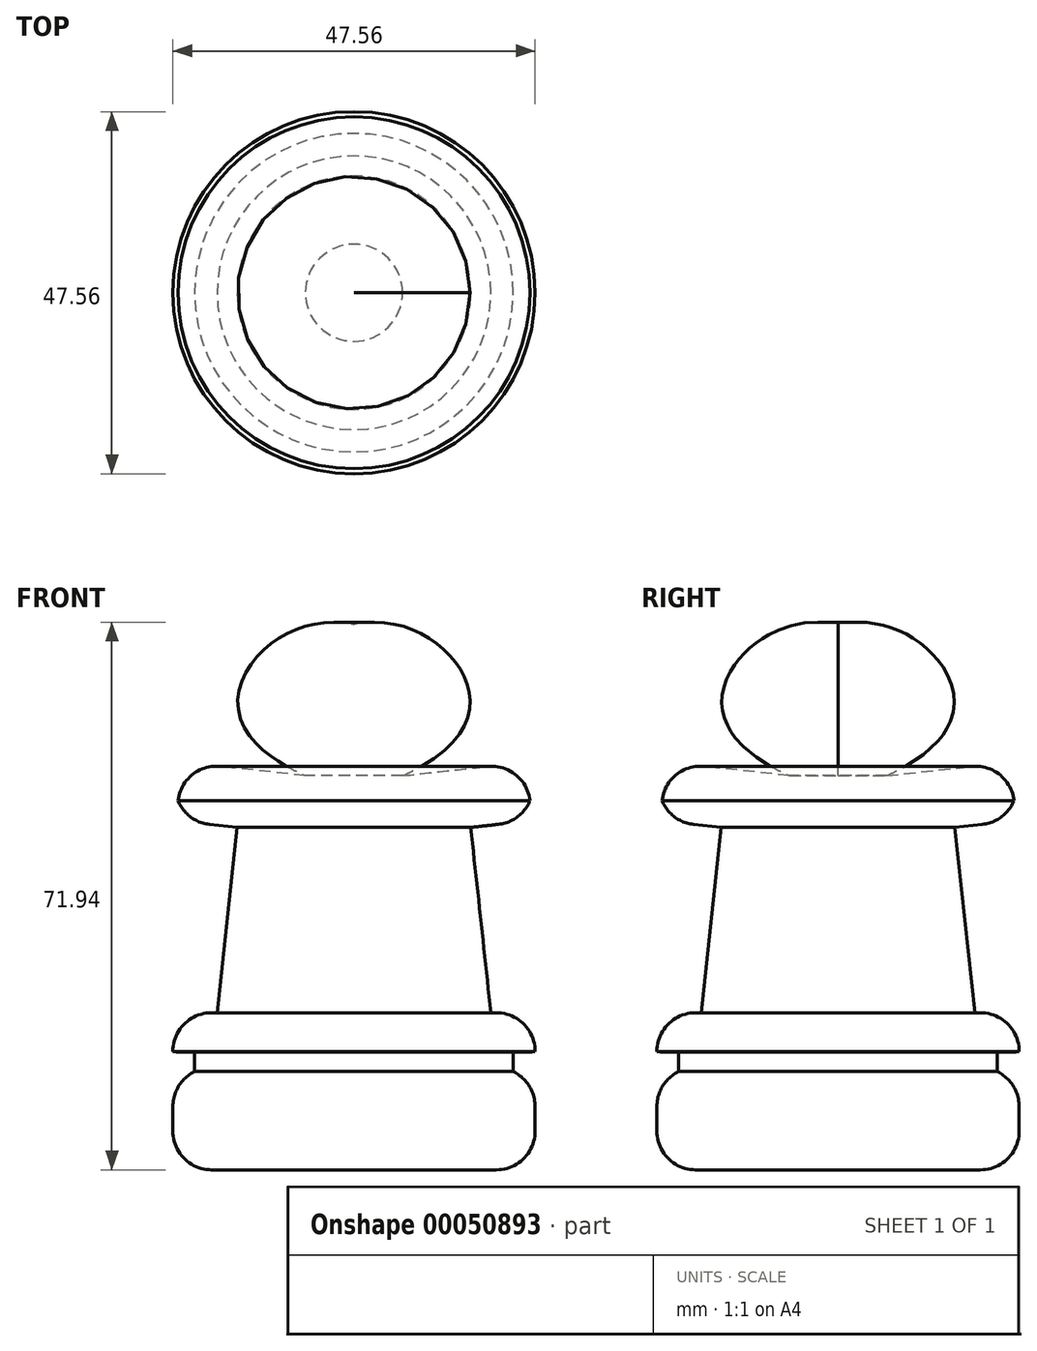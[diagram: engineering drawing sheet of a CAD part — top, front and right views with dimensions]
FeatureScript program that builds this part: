
annotation { "Feature Type Name" : "Feature", "Feature Type Description" : "" }
export const myFeature = defineFeature(function(context is Context, id is Id, definition is map)
    precondition{}
    {
        {
            var Q0;
            Q0=qCreatedBy(makeId("Front.planeOp"),FACE);
            var sketch = newSketch(context, id + "F0", { "sketchPlane" : qUnion([Q0])});
            skLineSegment(sketch, "E0", {"start": v(0, -65.77) * mm, "end": v(23.78, -65.77) * mm});
            skLineSegment(sketch, "E1", {"start": v(23.78, -65.77) * mm, "end": v(23.78, -52.87) * mm});
            skLineSegment(sketch, "E2", {"start": v(23.78, -52.87) * mm, "end": v(20.92, -52.87) * mm});
            skLineSegment(sketch, "E3", {"start": v(20.92, -52.87) * mm, "end": v(20.92, -50.3) * mm});
            skLineSegment(sketch, "E4", {"start": v(20.92, -50.3) * mm, "end": v(23.78, -50.3) * mm});
            skLineSegment(sketch, "E5", {"start": v(23.78, -50.3) * mm, "end": v(23.78, -45.13) * mm});
            skLineSegment(sketch, "E6", {"start": v(23.78, -45.13) * mm, "end": v(17.97, -45.13) * mm});
            skLineSegment(sketch, "E7", {"start": v(17.97, -45.13) * mm, "end": v(15.33, -20.78) * mm});
            skLineSegment(sketch, "E8", {"start": v(15.33, -20.78) * mm, "end": v(23.4, -19.9) * mm});
            skLineSegment(sketch, "E9", {"start": v(23.4, -19.9) * mm, "end": v(22.56, -12.23) * mm});
            skLineSegment(sketch, "E10", {"start": v(22.56, -12.23) * mm, "end": v(6.38, -13.99) * mm});
            skFitSpline(sketch, "E11", {"points": [v(6.38, -13.99) * mm, v(13.95, 0) * mm, v(0, 5.9) * mm], "startDerivative": vector(56.44, 25.22) * mm, "endDerivative": vector(-35.07, -7.52) * mm});
            skLineSegment(sketch, "E12", {"start": v(0, 5.9) * mm, "end": v(0, -65.77) * mm});
            skSolve(sketch);
        }
        {
            var Q0;
            Q0=makeQuery(id+"F0.imprint","IMPRINT",FACE,{"disambiguationData":[TD([[makeQuery(id+"F0.imprint","IMPRINT",EDGE,{"derivedFrom":sQuery(id+"F0.wireOp",EDGE,"E0")}),1.0]])]});
            var Q1;
            Q1=sQuery(id+"F0.wireOp",EDGE,"E6");
            var Q2;
            Q2=sQuery(id+"F0.wireOp",EDGE,"E5");
            var Q3;
            Q3=sQuery(id+"F0.wireOp",EDGE,"E0");
            var Q4;
            Q4=sQuery(id+"F0.wireOp",EDGE,"E1");
            var Q5;
            Q5=sQuery(id+"F0.wireOp",EDGE,"E12");
            var Q6;
            Q6=sQuery(id+"F0.wireOp",EDGE,"E11");
            var Q7;
            Q7=sQuery(id+"F0.wireOp",EDGE,"E10");
            var Q8;
            Q8=sQuery(id+"F0.wireOp",EDGE,"E9");
            var Q9;
            Q9=sQuery(id+"F0.wireOp",EDGE,"E8");
            var Q10;
            Q10=sQuery(id+"F0.wireOp",EDGE,"E7");
            var Q11;
            Q11=sQuery(id+"F0.wireOp",EDGE,"E4");
            var Q12;
            Q12=sQuery(id+"F0.wireOp",EDGE,"E3");
            var Q13;
            Q13=sQuery(id+"F0.wireOp",EDGE,"E2");
            var Q14;
            Q14=sQuery(id+"F0.wireOp",EDGE,"E12");
            revolve(context, id + "F1", {"entities" : qUnion([Q0]), "surfaceEntities" : qUnion([Q1, Q2, Q3, Q4, Q5, Q6, Q7, Q8, Q9, Q10, Q11, Q12, Q13]), "axis" : qUnion([Q14]), "revolveType" : RevolveType.FULL});
        }
        {
            var Q0;
            Q0=makeQuery(id+"F1.opRevolve","SWEPT_EDGE",EDGE,{"disambiguationData":[OSD([sQuery(id+"F0.wireOp",EDGE,"E9"),sQuery(id+"F0.wireOp",EDGE,"E10")])]});
            fillet(context, id + "F2", {"entities" : qUnion([Q0]), "radius" : 5.08 * mm, "tangentPropagation" : true, "allowEdgeOverflow" : false});
        }
        {
            var Q0;
            Q0=makeQuery(id+"F1.opRevolve","SWEPT_EDGE",EDGE,{"disambiguationData":[OSD([sQuery(id+"F0.wireOp",EDGE,"E8"),sQuery(id+"F0.wireOp",EDGE,"E9")])]});
            fillet(context, id + "F3", {"entities" : qUnion([Q0]), "radius" : 5.08 * mm, "tangentPropagation" : true, "allowEdgeOverflow" : false});
        }
        {
            var Q0;
            Q0=makeQuery(id+"F1.opRevolve","SWEPT_EDGE",EDGE,{"disambiguationData":[OSD([sQuery(id+"F0.wireOp",EDGE,"E5"),sQuery(id+"F0.wireOp",EDGE,"E6")])]});
            fillet(context, id + "F4", {"entities" : qUnion([Q0]), "radius" : 5.08 * mm, "tangentPropagation" : true, "allowEdgeOverflow" : false});
        }
        {
            var Q0;
            Q0=makeQuery(id+"F1.opRevolve","SWEPT_EDGE",EDGE,{"disambiguationData":[OSD([sQuery(id+"F0.wireOp",EDGE,"E4"),sQuery(id+"F0.wireOp",EDGE,"E5")])]});
            fillet(context, id + "F5", {"entities" : qUnion([Q0]), "radius" : 5.08 * mm, "tangentPropagation" : true, "allowEdgeOverflow" : false});
        }
        {
            var Q0;
            Q0=makeQuery(id+"F1.opRevolve","SWEPT_FACE",FACE,{"disambiguationData":[OSD([sQuery(id+"F0.wireOp",EDGE,"E1")])]});
            fillet(context, id + "F6", {"entities" : qUnion([Q0]), "radius" : 5.08 * mm, "tangentPropagation" : true, "allowEdgeOverflow" : false});
        }
    });
